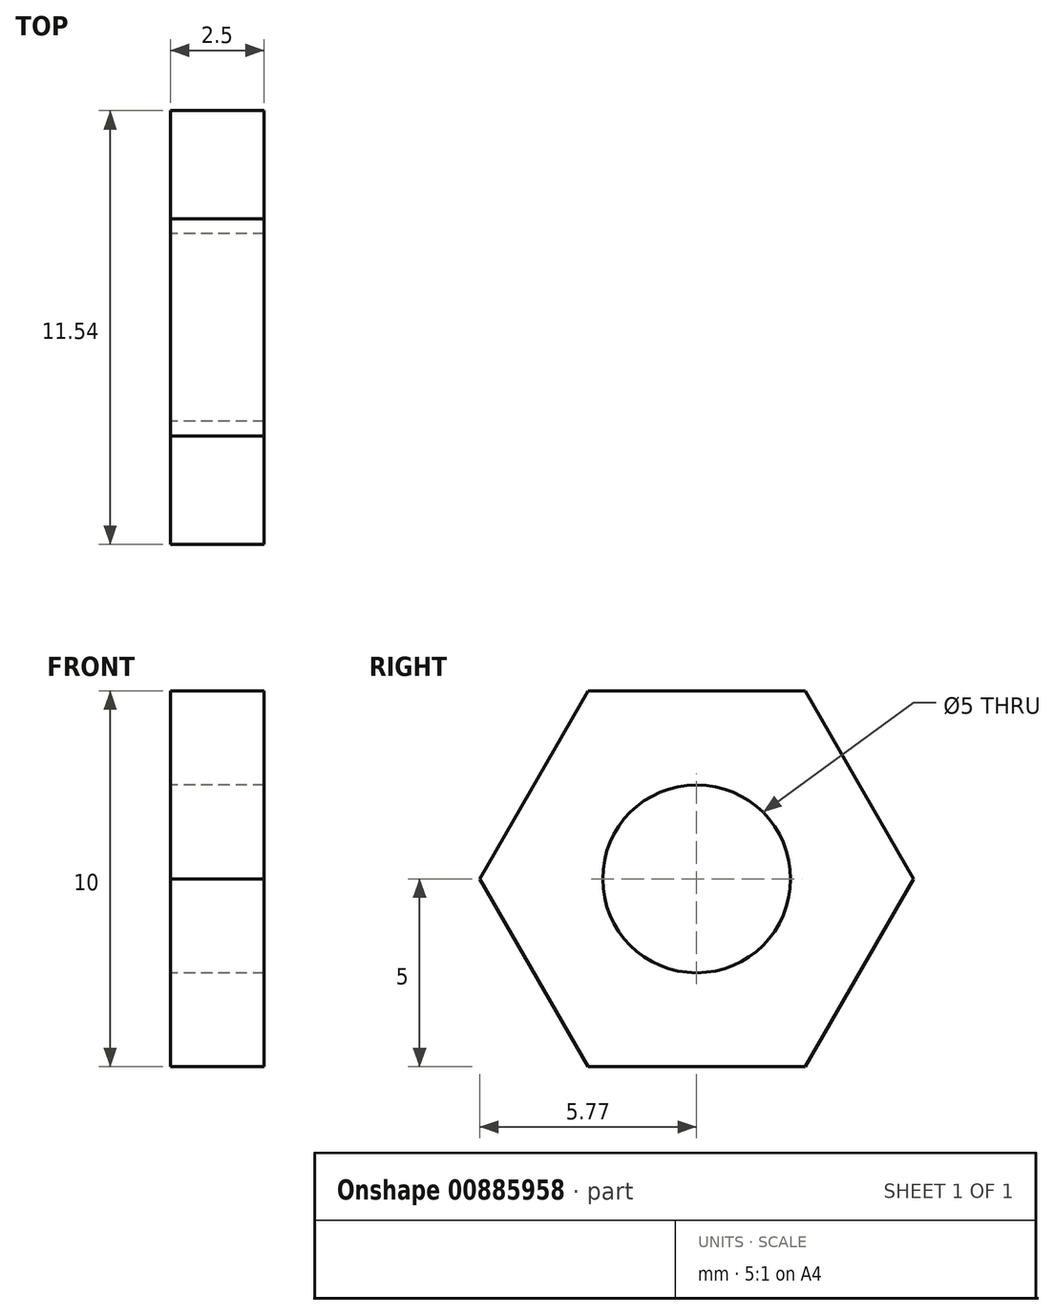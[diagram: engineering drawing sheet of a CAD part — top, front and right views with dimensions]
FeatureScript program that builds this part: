
annotation { "Feature Type Name" : "Feature", "Feature Type Description" : "" }
export const myFeature = defineFeature(function(context is Context, id is Id, definition is map)
    precondition{}
    {
        {
            var Q0;
            Q0=qCreatedBy(makeId("Right.planeOp"),FACE);
            var sketch = newSketch(context, id + "F0", { "sketchPlane" : qUnion([Q0])});
            skCircle(sketch, "E0.cCircle", {"center": v(0, 0) * mm, "radius": 5 * mm, "construction": true});
            skLineSegment(sketch, "E0.0", {"start": v(-2.89, 5) * mm, "end": v(2.89, 5) * mm});
            skLineSegment(sketch, "E0.1", {"start": v(2.89, 5) * mm, "end": v(5.77, 0) * mm});
            skLineSegment(sketch, "E0.2", {"start": v(5.77, 0) * mm, "end": v(2.89, -5) * mm});
            skLineSegment(sketch, "E0.3", {"start": v(2.89, -5) * mm, "end": v(-2.89, -5) * mm});
            skLineSegment(sketch, "E0.4", {"start": v(-2.89, -5) * mm, "end": v(-5.77, 0) * mm});
            skLineSegment(sketch, "E0.5", {"start": v(-5.77, 0) * mm, "end": v(-2.89, 5) * mm});
            skPoint(sketch, "E0.0.midPoint", {"position": v(0, 5) * mm});
            skCircle(sketch, "E1", {"center": v(0, 0) * mm, "radius": 2.5 * mm});
            skSolve(sketch);
        }
        {
            var Q0;
            Q0 = qSketchRegion(id + "F0", true);
            extrude(context, id + "F1", {"entities" : qUnion([Q0]), "depth" : 2.5 * mm, "offsetDistance" : 25 * mm});
        }
    });
